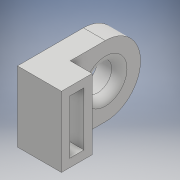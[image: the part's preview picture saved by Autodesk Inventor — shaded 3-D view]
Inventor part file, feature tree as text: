
AUTODESK INVENTOR PART (.ipt)
format: ipt  version: 2018 (Build 220112000, 112)  size: 141,824 bytes
history: native  units: mm
features: extrude x3, sketch x3, fillet x2
ambient origin geometry x8: Origin, YZ Plane, XZ Plane, XY Plane, X Axis, Y Axis, Z Axis, Center Point
bodies: Solid1 (feature_tree)
feature tree (8):
  extrude  "Extrusion1"  Depth=12.25mm
  extrude  "Extrusion2"  Depth=16.0mm
  extrude  "Extrusion3"  Depth=5.0mm
  fillet  "Fillet1"  Radius=16.0mm
  fillet  "Fillet2"  Radius=6.35mm
  sketch  "Sketch1"  dims[d0=3.25mm d1=12.25mm]
  sketch  "Sketch2"  dims[d2=7.0mm d3=16.0mm]
  sketch  "Sketch3"  dims[d4=10.0mm d5=0.0mm d6=5.0mm d7=16.0mm d8=0.0mm d9=6.35mm d10=16.0mm d11=0.0mm d12=8.0mm d13=1.75mm]
